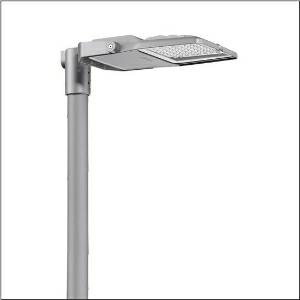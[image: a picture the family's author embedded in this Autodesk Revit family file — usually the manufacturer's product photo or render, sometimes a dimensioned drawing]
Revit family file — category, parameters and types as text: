
# Revit family: floodlight_fl_21_mini___pl33t_5xa7775d2f3a_2fb5
name_source: partatom
category: Lighting Fixtures
units: mm (PartAtom-declared; Revit-internal decimal feet)

## family parameters
Cut with Voids When Loaded = No
Host = Face
Light Source = No
Part Type = Normal
Room Calculation Point = No
Round Connector Dimension = Use Diameter
Shared = No

## types (1)
- --- (1 x LED, 17630 lm, 142.9 W, 3000K)
    Apparent Load = 143 VA
    CIE Flux Codes = 26 75 99 100 100
    Color Rendering = 70
    Color Temperature = 3000K
    Default Elevation = 1800 mm
    Description = Floodlight FL 21 mini, floodlight, primary light control with lens, of PMMA, primary optical cover: protective disc, of toughened safety glass, transparent, light distribution: PL33T, light emission: direct distribution, installation type: surface-mounted, LED, High Power LED, rated luminous flux: 17.630lm, luminous efficacy: 123lm/W, light colour: 730, colour temperature: 3000K, control gear: ECG Smart Interface, control: flexible luminous flux parameterisation, time-dependent luminous flux control, constant luminous flux control, overheat protection, presetting dimming logarithmic, with terminal, 6-pole, mains connection: 220..240V, AC, 50/60Hz, start of lifetime: 143W, end of lifetime: 151W, reduction: 63W, luminaire housing, of diecast aluminium, powder-coated, Siteco® metallic grey (DB 702S), corrosivity category C5 according to DIN EN ISO 12944, mast bracket, of steel, galvanised, powder-coated, Siteco® metallic grey (DB 702S), protection rating (complete): IP66, insulation class (complete): insulation class II (safety insulation), certification: CE, ENEC, VDE, protection symbol: D, impact resistance: IK08, permissible operating ambient temperature: -40..+40°C, permissible operating ambient temperature for outdoor applications: -40..+50°C, standard: DIN EN 12944, packaging unit: 1 piece

Light Distribution: PL33T
    Height = 70 mm
    Lamp = 1 x LED
    Lamp Light Flux = 17630 lm
    Lamp Power = 142.9 W
    Lamp count = 1
    Length = 485 mm
    Luminous efficacy = 123 lm/W
    Manufacturer = Siteco
    ModVariant = No
    Model = 5XA7775D2F3A
    Number of Poles = 1
    OnlyDefault = Yes
    Power Factor = 1
    Product Name = Floodlight FL 21 mini | PL33T
    Product group = floodlight | pylon top
    ProductGroupID = 6101
    Protection Class = Protection class II
    Protection Degree = IP 66
    RLX_Detail_Level = 1
    RlxData = <blob elided: 100961 chars, md5=7e6194d6>
    Socket = socket
    Standby Power = 0 W
    System Light Flux = 17630 lm
    System Power = 143 W
    Type Comments = factory setting: luminous flux: 100 % | dim-lin: 254 | 730 mA
    Type Image = l_1007125.jpg
    URL = http://relux.com
    VarID = @adj_058495
    Voltage = 0 V
    Weight = 0.00 kg
    Width = 337 mm

## geometry (parser evidence)
native form markers: Blend x4, Sweep x10
no freeform markers — native parametric forms only
